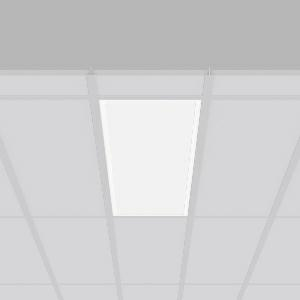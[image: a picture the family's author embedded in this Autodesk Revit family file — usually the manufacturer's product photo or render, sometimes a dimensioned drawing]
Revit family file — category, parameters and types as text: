
# Revit family: sidelite_eco_312365_002_1_790_4d02
name_source: partatom
category: Lighting Fixtures
units: mm (PartAtom-declared; Revit-internal decimal feet)

## family parameters
Cut with Voids When Loaded = No
Host = Face
Light Source = No
Part Type = Normal
Room Calculation Point = No
Round Connector Dimension = Use Diameter
Shared = No

## types (1)
- MultiLumen 1 (1 x LED Modul 840, 3500 lm, 4000)
    Apparent Load = 29 VA
    CIE Flux Codes = 47 79 96 100 100
    Color Rendering = 80
    Color Temperature = 4000
    Default Elevation = 1800 mm
    Description = Series: SIDELITE ECO
Highly economical recessed luminaire with progressive LED technology. Frame made of aluminium, powder-coated. Diffuser: plastic, opal. Lightguide and diffuser made of non-yellowing plastic (PMMA). Lateral light emission (RZB SIDELITE technology) for homogeneous light distribution. External driver. External driver with simple plug-in locking system and extended converter connecting cable to luminaire (1.90 m). MultiLumen: 4 steps adjustable luminous flux. Factory setting is the lowest offered step. Luminaire can be used with accessories (to be ordered separately) for recessed, surface mounting or as pendant luminaire. Qualified for use in the food and drink industry. 
Colour: white
Length: 1195 mm
Width: 295 mm
Cut-out length: 1180 mm
Cut-out width: 280 mm
Recess height: 160 mm
Luminaire: recess height: 37 mm
Lamp: LED
Socket: without socket
Colour temperature: 4000K
Colour rendering index (CRI): 80
System power: 29 W
Rated luminous flux: 3500 lm
Luminous efficiency: 121 lm/W
System power 2: 33 W
Rated luminous flux 2: 3850 lm
Luminous efficiency 2: 117 lm/W
System power 3: 35 W
Rated luminous flux 3: 4050 lm
Luminous efficiency 3: 116 lm/W
System power 4: 38 W
Rated luminous flux 4: 4400 lm
Luminous efficiency 4: 116 lm/W
Control gear: Regulated power supply
Protection class: II
Type of protection: IP 40
    Height = 0 mm  [stored 0 ft]
    Lamp = 1 x LED Modul 840
    Lamp Light Flux = 3500 lm
    Lamp count = 1
    Length = 1195 mm
    Lifetime = 50000 h
    Luminous efficacy = 121 lm/W
    Manufacturer = RZB
    ModVariant = No
    Model = 312365.002.1.790
    Mounting Place = Ceiling
    Mounting Type = Recessed
    Number of Poles = 1
    OnlyDefault = Yes
    Power Factor = 1
    Product Name = SIDELITE ECO
    Product group = Recessed modular luminaires
    ProductGroupID = 406
    Protection Class = Protection class II
    Protection Degree = IP 20
    RLX_Detail_Level = 1
    RLX_Emergency_Light_Flux = 0 lm
    RLX_Emergency_Type = 0
    RLX_Emergency_Type_DB = No
    RlxData = <blob elided: 30905 chars, md5=fcf08328>
    Socket = socket
    Standby Power = 0 W
    System Light Flux = 3500 lm
    System Power = 29 W
    Type Comments = MultiLumen 1
    Type Image = 312365.002.jpg
    URL = http://relux.com
    VarID = multilumen_1
    Voltage = 230 V
    Voltage Range = 220-240 V
    Weight = 0.00 kg
    Width = 295 mm

note: [stored X ft] marks values corroborated as IEEE doubles in the binary element streams (Revit-internal decimal feet)

## geometry (parser evidence)
native form markers: Blend x4, Sweep x9
no freeform markers — native parametric forms only
